# Revit family: 0045060
name_source: partatom
category: Lighting Fixtures
revit_build: Autodesk Revit 2017 (Build: 20190507_1515(x64)
units: mm (PartAtom-declared; Revit-internal decimal feet)

## family parameters
Cut with Voids When Loaded = No
Host = Face
Light Source = Yes
OmniClass Number = 23.80.70.00
OmniClass Title = Lighting
Part Type = Normal
Room Calculation Point = No
Round Connector Dimension = Use Diameter
Shared = No

## types (1)
- 0045060 OPTIX S 1200 2L D/I TW WHT SSC EM
    Apparent Load = 35 VA
    Assembly Code = D5020200
    AssetType = Fixed
    ClassificationName = Uniclass2015
    ClassificationValue = EF_70_80
    Color Filter = 16777215
    Cost = 0 $
    Default Elevation = 1219 mm
    Description = OPTIX S 1200x200 2 LINE D/I TW WHITE SSC EM is a high efficacy low glare luminaire for office and education applications. Direct / Indirect lighting with 80% downlight and 20% uplight ratio for ceiling suspended mounting. Size: 1129x200x45mm. White plastic low glare optics in 2 lines configuration. White RAL9016 fixture body. SylSmart Stand-alone Office control for colour tuning. 3hr maintained emergency version. Tunable White LED, CRI>80, chromaticity tolerance of 3-step MacAdam ellipse. Luminous flux 3900lm. Power consumption 35W. Luminaire efficacy 111lm/W. Lumen maintenance of L90B50 = 39000h. UGR<19, Luminance at 65°<3000 Cd/m2, IK07, IP20. Photobiological safety risk group 0. Electrical protection Class I. Glow wire test 850°C.
    Dimming Lamp Color Temperature Shift = <None>
    DocumentationLiterature = http://www.sylvania-lighting.com
    ElectricShockClassification = Class I
    Emit Shape Visible in Rendering = No
    Emit from Circle Diameter = 610 mm
    Height = 50 mm  [stored 0.164042 ft]
    IfcExportAs = IfcLightFixtureType
    IfcExportType = IfcLightFixtureType
    ImpactProtectionIndex = IK07
    IngressProtection = IP20
    Keynote = 16500
    Lamp = LED
    LampColourRenderingIndex = 80
    LampColourTemperature = 3000 K
    LampMacAdamStep = 3
    LampNominalLuminous = 3900 lm
    LampsType = LED
    Length = 1130 mm  [stored 3.70735 ft]
    LuminousEfficacy = 111 lm/W
    Manufacturer = Feilo Sylvania
    ManufacturerName = Feilo Sylvania
    Material = steel housing, pc polycarbonate diffuser
    Material_1_SYL = <By Category>
    Material_2_SYL = <By Category>
    Material_3_SYL = <By Category>
    Material_4_SYL = <By Category>
    Model = OPTIX S 1200x200 2 LINE D/I TW WHITE SSC EM
    ModelNumber = 0045060
    ModelReference = OPTIX S 1200x200 2 LINE D/I TW WHITE SSC EM
    Name = OPTIX S 1200x200 2 LINE D/I TW WHITE SSC EM
    NominalDepth = 200 mm  [stored 0.656168 ft]
    NominalHeight = 45 mm  [stored 0.147638 ft]
    NominalLength = 1129 mm  [stored 3.70407 ft]
    Photometric Web File = 0045059.ies
    PowerConsumption = 35 W
    PowerFactor = 0.95
    Tilt Angle = -90.00°
    Type Image = <None>
    TypeName = OPTIX S 1200x200 2 LINE D/I TW WHITE SSC EM
    URL = http://www.sylvania-lighting.com
    Voltage = 0 V
    Weight = 4.8 kg
    Width = 200 mm  [stored 0.656168 ft]

note: [stored X ft] marks values corroborated as IEEE doubles in the binary element streams (Revit-internal decimal feet)

## geometry (parser evidence)
native form markers: Sweep x3
no freeform markers — native parametric forms only
